# Revit family: xxxDrinking_Fountain-Bottle_Filler-Acorn-LR1671-1-03
name_source: partatom
category: Plumbing Fixtures
units: mm (PartAtom-declared; Revit-internal decimal feet)

## family parameters
Cut with Voids When Loaded = Yes
Host = Face
OmniClass Number = 23.65.70.14.11
OmniClass Title = Drinking Fountains/Coolers
Part Type = Normal
Room Calculation Point = No
Round Connector Dimension = Use Diameter
Shared = Yes

## types (1)
- LR1671-1-03
    -BRS Optional Brass Body Valve = No
    -EG Optional Enviro-Glaze = No
    -MT Optional Metal Template = No
    -PT Optional P-Trap Waste = Yes
    -SW Optional Wall Sleeve = No
    -TG Optional 12 Gage Cabinet = No
    ADA Compliant = Yes
    Assembly Code = D2010810
    CW Connection = Yes
    CWFU = 1.5
    Default Elevation = 0"
    Description = Secur-Care® Ligature-Resistant, Recessed Bottle Filler and Bubbler
    Finish = Stainless Steel-Acorn-Type 304-14 Gauge-Satin
    Flow Rate = 0.7 GPM (2.65 LPM)
    HW Connection = No
    HWFU = 0
    Height = 34 5/8"
    Height AFF- Bottle Filler = 47"
    Height AFF- Water Bubbler = 36"
    Installation Type = Wall Mounted/Recessed
    Lead-Free NSF61, Section 9 & CHSC 116875 = Yes
    Length = 10"
    Manufacturer = Acorn
    Material = Stainless Steel-Acorn-Type 304-14 Gauge-Satin
    Model = LR1671-1-03
    Pipe Connector Placement = 1"
    Price = Prices may vary. Please consult Manufacturer Representative for most up-to-date price list.
    Product Documentation Link = https://www.acorneng.com
    Product Page URL = https://www.acorneng.com
    Required Valve Activation Force = Less than 5 lbs
    Standard Waste Outlet = No
    URL = https://www.acorneng.com
    Vent Connection = No
    WFU = 2
    Waste Connection = Yes
    Waste Connection Diameter = 1 1/2"
    Waste Outlet Option = 3 1/4"
    Width = 19"
    Width- Cabinet = 15"

## geometry (parser evidence)
native form markers: Sweep x3
no freeform markers — native parametric forms only
